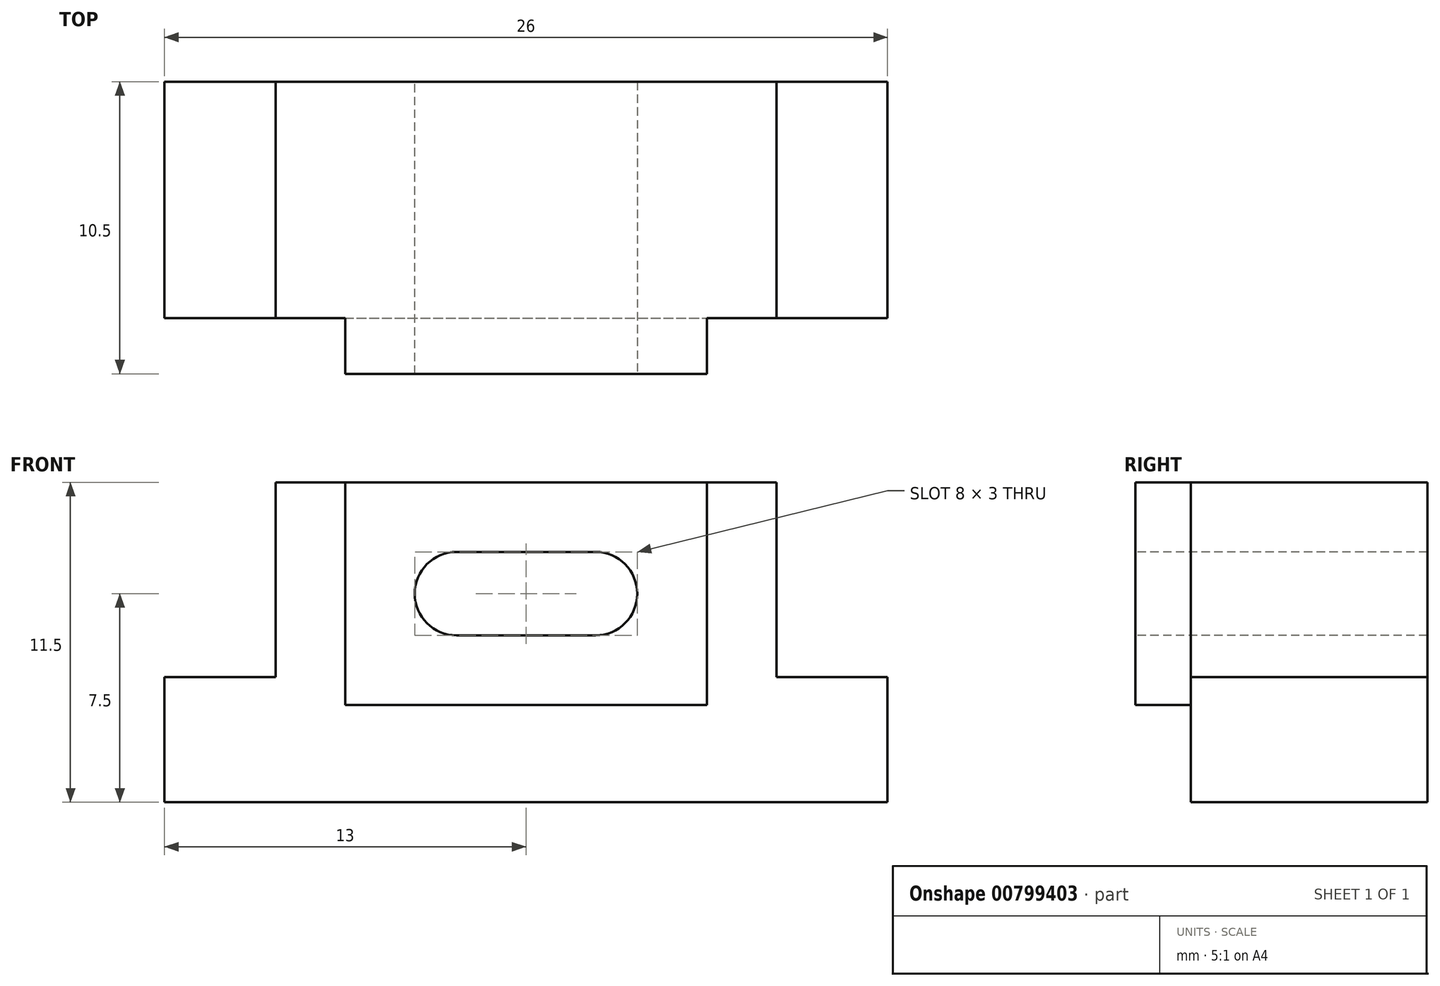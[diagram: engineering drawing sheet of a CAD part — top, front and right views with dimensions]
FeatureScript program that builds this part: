
annotation { "Feature Type Name" : "Feature", "Feature Type Description" : "" }
export const myFeature = defineFeature(function(context is Context, id is Id, definition is map)
    precondition{}
    {
        {
            var Q0;
            Q0=qCreatedBy(makeId("Front.planeOp"),FACE);
            var sketch = newSketch(context, id + "F0", { "sketchPlane" : qUnion([Q0])});
            skLineSegment(sketch, "E0.bottom", {"start": v(-13, 0) * mm, "end": v(13, 0) * mm});
            skLineSegment(sketch, "E0.top", {"start": v(-13, 4.5) * mm, "end": v(13, 4.5) * mm});
            skLineSegment(sketch, "E0.left", {"start": v(-13, 0) * mm, "end": v(-13, 4.5) * mm});
            skLineSegment(sketch, "E0.right", {"start": v(13, 0) * mm, "end": v(13, 4.5) * mm});
            skLineSegment(sketch, "E1.bottom", {"start": v(-9, 4.5) * mm, "end": v(9, 4.5) * mm});
            skLineSegment(sketch, "E1.top", {"start": v(-9, 11.5) * mm, "end": v(9, 11.5) * mm});
            skLineSegment(sketch, "E1.left", {"start": v(-9, 4.5) * mm, "end": v(-9, 11.5) * mm});
            skLineSegment(sketch, "E1.right", {"start": v(9, 4.5) * mm, "end": v(9, 11.5) * mm});
            skSolve(sketch);
        }
        {
            var Q0;
            Q0 = qSketchRegion(id + "F0", true);
            extrude(context, id + "F1", {"entities" : qUnion([Q0]), "endBound" : BoundingType.SYMMETRIC, "depth" : 8.5 * mm, "offsetDistance" : 25 * mm});
        }
        {
            var Q0;
            Q0=makeQuery(id+"F1.opExtrude","CAP_FACE",FACE,{"disambiguationData":[OSD([sQuery(id+"F0.wireOp",EDGE,"E0.bottom"),sQuery(id+"F0.wireOp",EDGE,"E0.top"),sQuery(id+"F0.wireOp",EDGE,"E0.left"),sQuery(id+"F0.wireOp",EDGE,"E0.right"),sQuery(id+"F0.wireOp",EDGE,"E1.top"),sQuery(id+"F0.wireOp",EDGE,"E1.left"),sQuery(id+"F0.wireOp",EDGE,"E1.right")])],"isStart":false});
            var sketch = newSketch(context, id + "F2", { "sketchPlane" : qUnion([Q0])});
            skLineSegment(sketch, "E2.bottom", {"start": v(-6.5, 11.5) * mm, "end": v(6.5, 11.5) * mm});
            skLineSegment(sketch, "E2.top", {"start": v(-6.5, 3.5) * mm, "end": v(6.5, 3.5) * mm});
            skLineSegment(sketch, "E2.left", {"start": v(-6.5, 11.5) * mm, "end": v(-6.5, 3.5) * mm});
            skLineSegment(sketch, "E2.right", {"start": v(6.5, 11.5) * mm, "end": v(6.5, 3.5) * mm});
            skSolve(sketch);
        }
        {
            var Q0;
            Q0 = qSketchRegion(id + "F2", true);
            var Q1;
            Q1=makeQuery(id+"F2.imprint","IMPRINT",FACE,{"disambiguationData":[TD([[makeQuery(id+"F2.imprint","IMPRINT",EDGE,{"derivedFrom":sQuery(id+"F2.wireOp",EDGE,"E2.bottom")}),-1.0]])]});
            extrude(context, id + "F3", {"entities" : qUnion([Q0, Q1]), "operationType" : NewBodyOperationType.ADD, "depth" : 2 * mm, "offsetDistance" : 25 * mm});
        }
        {
            var Q0;
            Q0=makeQuery(id+"F3.opExtrude","CAP_FACE",FACE,{"disambiguationData":[OSD([sQuery(id+"F2.wireOp",EDGE,"E2.bottom"),sQuery(id+"F2.wireOp",EDGE,"E2.top"),sQuery(id+"F2.wireOp",EDGE,"E2.left"),sQuery(id+"F2.wireOp",EDGE,"E2.right")])],"isStart":false});
            var sketch = newSketch(context, id + "F4", { "sketchPlane" : qUnion([Q0])});
            skLineSegment(sketch, "E3.bottom", {"start": v(4, 6) * mm, "end": v(-4, 6) * mm});
            skLineSegment(sketch, "E3.top", {"start": v(4, 9) * mm, "end": v(-4, 9) * mm});
            skLineSegment(sketch, "E3.left", {"start": v(4, 6) * mm, "end": v(4, 9) * mm});
            skLineSegment(sketch, "E3.right", {"start": v(-4, 6) * mm, "end": v(-4, 9) * mm});
            skPoint(sketch, "E3.middle", {"position": v(0, 7.5) * mm});
            skLineSegment(sketch, "E4", {"start": v(-6.5, 7.5) * mm, "end": v(6.5, 7.5) * mm, "construction": true});
            skSolve(sketch);
        }
        {
            var Q0;
            Q0=makeQuery(id+"F4.imprint","IMPRINT",FACE,{"disambiguationData":[TD([[makeQuery(id+"F4.imprint","IMPRINT",EDGE,{"derivedFrom":sQuery(id+"F4.wireOp",EDGE,"E3.bottom")}),-1.0]])]});
            var Q1;
            Q1=makeQuery(id+"F1.opExtrude","CAP_FACE",FACE,{"disambiguationData":[OSD([sQuery(id+"F0.wireOp",EDGE,"E0.bottom"),sQuery(id+"F0.wireOp",EDGE,"E0.top"),sQuery(id+"F0.wireOp",EDGE,"E0.left"),sQuery(id+"F0.wireOp",EDGE,"E0.right"),sQuery(id+"F0.wireOp",EDGE,"E1.top"),sQuery(id+"F0.wireOp",EDGE,"E1.left"),sQuery(id+"F0.wireOp",EDGE,"E1.right")])],"isStart":true});
            extrude(context, id + "F5", {"entities" : qUnion([Q0]), "operationType" : NewBodyOperationType.REMOVE, "endBound" : BoundingType.UP_TO_SURFACE, "oppositeDirection" : true, "depth" : 25 * mm, "endBoundEntityFace" : qUnion([Q1]), "offsetDistance" : 25 * mm});
        }
        {
            var Q0;
            Q0=makeQuery(id+"F5.boolean.opBoolean","COPY",EDGE,{"derivedFrom":makeQuery(id+"F5.opExtrude","SWEPT_EDGE",EDGE,{"disambiguationData":[OSD([sQuery(id+"F4.wireOp",EDGE,"E3.bottom"),sQuery(id+"F4.wireOp",EDGE,"E3.right")])]})});
            var Q1;
            Q1=makeQuery(id+"F5.boolean.opBoolean","COPY",EDGE,{"derivedFrom":makeQuery(id+"F5.opExtrude","SWEPT_EDGE",EDGE,{"disambiguationData":[OSD([sQuery(id+"F4.wireOp",EDGE,"E3.top"),sQuery(id+"F4.wireOp",EDGE,"E3.right")])]})});
            var Q2;
            Q2=makeQuery(id+"F5.boolean.opBoolean","COPY",EDGE,{"derivedFrom":makeQuery(id+"F5.opExtrude","SWEPT_EDGE",EDGE,{"disambiguationData":[OSD([sQuery(id+"F4.wireOp",EDGE,"E3.bottom"),sQuery(id+"F4.wireOp",EDGE,"E3.left")])]})});
            var Q3;
            Q3=makeQuery(id+"F5.boolean.opBoolean","COPY",EDGE,{"derivedFrom":makeQuery(id+"F5.opExtrude","SWEPT_EDGE",EDGE,{"disambiguationData":[OSD([sQuery(id+"F4.wireOp",EDGE,"E3.top"),sQuery(id+"F4.wireOp",EDGE,"E3.left")])]})});
            fillet(context, id + "F6", {"entities" : qUnion([Q0, Q1, Q2, Q3]), "radius" : 1.5 * mm, "tangentPropagation" : true, "allowEdgeOverflow" : false});
        }
    });
